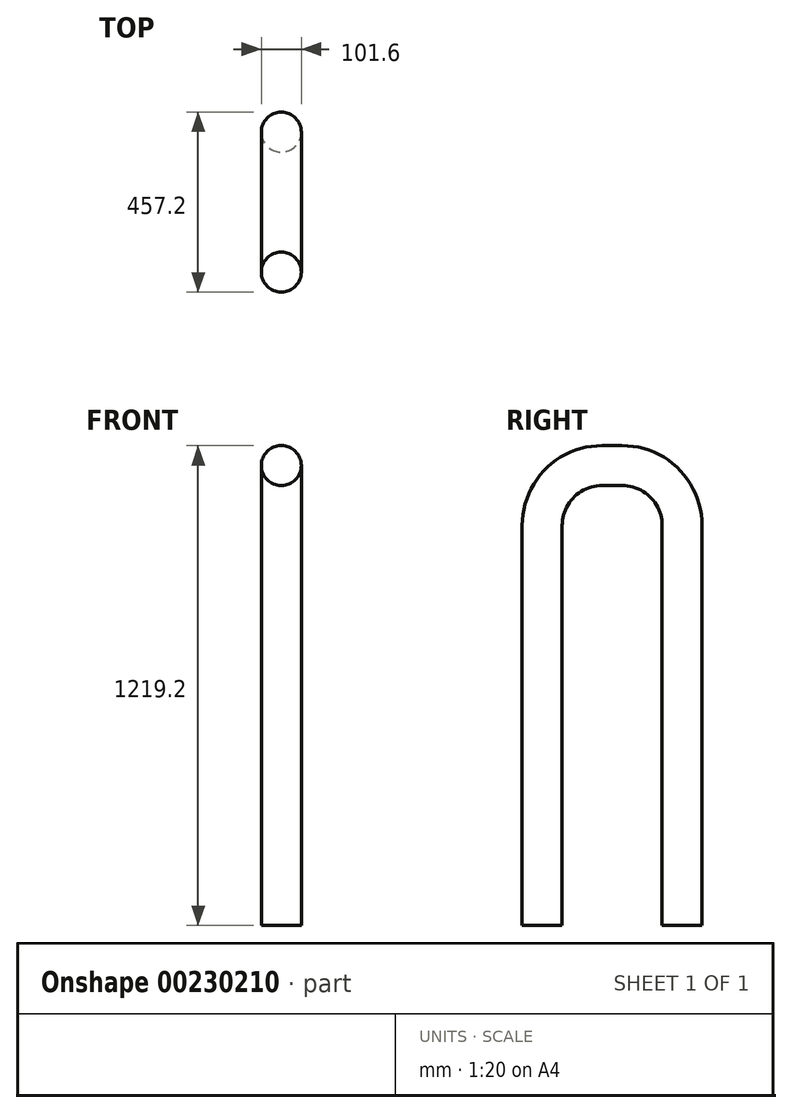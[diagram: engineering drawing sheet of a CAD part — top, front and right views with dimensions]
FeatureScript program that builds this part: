
annotation { "Feature Type Name" : "Feature", "Feature Type Description" : "" }
export const myFeature = defineFeature(function(context is Context, id is Id, definition is map)
    precondition{}
    {
        {
            var Q0;
            Q0=qCreatedBy(makeId("Right.planeOp"),FACE);
            var sketch = newSketch(context, id + "F0", { "sketchPlane" : qUnion([Q0])});
            skLineSegment(sketch, "E0", {"start": v(-207.98, 0) * mm, "end": v(-207.98, 1111.25) * mm});
            skLineSegment(sketch, "E1", {"start": v(-201.63, 1117.6) * mm, "end": v(46.02, 1117.6) * mm});
            skLineSegment(sketch, "E2", {"start": v(46.02, 1117.6) * mm, "end": v(46.02, 0) * mm});
            skLineSegment(sketch, "E3", {"start": v(46.02, 0) * mm, "end": v(147.62, 0) * mm});
            skLineSegment(sketch, "E4", {"start": v(147.62, 0) * mm, "end": v(147.62, 1219.2) * mm});
            skLineSegment(sketch, "E5", {"start": v(147.62, 1219.2) * mm, "end": v(-309.58, 1219.2) * mm});
            skLineSegment(sketch, "E6", {"start": v(-309.58, 1219.2) * mm, "end": v(-309.58, 0) * mm});
            skLineSegment(sketch, "E7", {"start": v(-309.58, 0) * mm, "end": v(-207.98, 0) * mm});
            skPoint(sketch, "E8.visualSharp", {"position": v(-207.98, 1117.6) * mm});
            skLineSegment(sketch, "E9", {"start": v(-207.98, 1111.25) * mm, "end": v(-207.98, 1117.6) * mm});
            skLineSegment(sketch, "E10", {"start": v(-201.63, 1117.6) * mm, "end": v(-207.98, 1117.6) * mm});
            skSolve(sketch);
        }
        {
            var Q0;
            Q0=qSketchRegion(id+"F0",true);
            extrude(context, id + "F1", {"entities" : qUnion([Q0]), "depth" : 101.6 * mm});
        }
        {
            var Q0;
            Q0=makeQuery(id+"F1.opExtrude","SWEPT_EDGE",EDGE,{"disambiguationData":[OSD([sQuery(id+"F0.wireOp",EDGE,"E9"),sQuery(id+"F0.wireOp",EDGE,"E10")])]});
            var Q1;
            Q1=makeQuery(id+"F1.opExtrude","SWEPT_EDGE",EDGE,{"disambiguationData":[OSD([sQuery(id+"F0.wireOp",EDGE,"E1"),sQuery(id+"F0.wireOp",EDGE,"E2")])]});
            fillet(context, id + "F2", {"entities" : qUnion([Q0, Q1]), "radius" : 101.6 * mm, "tangentPropagation" : true, "allowEdgeOverflow" : false});
        }
        {
            var Q0;
            Q0=makeQuery(id+"F1.opExtrude","SWEPT_EDGE",EDGE,{"disambiguationData":[OSD([sQuery(id+"F0.wireOp",EDGE,"E5"),sQuery(id+"F0.wireOp",EDGE,"E6")])]});
            var Q1;
            Q1=makeQuery(id+"F1.opExtrude","SWEPT_EDGE",EDGE,{"disambiguationData":[OSD([sQuery(id+"F0.wireOp",EDGE,"E4"),sQuery(id+"F0.wireOp",EDGE,"E5")])]});
            fillet(context, id + "F3", {"entities" : qUnion([Q0, Q1]), "radius" : 203.2 * mm, "tangentPropagation" : true, "allowEdgeOverflow" : false});
        }
        {
            var Q0;
            Q0=makeQuery(id+"F1.opExtrude","CAP_EDGE",EDGE,{"disambiguationData":[OSD([sQuery(id+"F0.wireOp",EDGE,"E0"),sQuery(id+"F0.wireOp",EDGE,"E9")])],"isStart":false});
            var Q1;
            Q1=makeQuery(id+"F1.opExtrude","CAP_EDGE",EDGE,{"disambiguationData":[OSD([sQuery(id+"F0.wireOp",EDGE,"E6")])],"isStart":false});
            var Q2;
            Q2=makeQuery(id+"F1.opExtrude","CAP_EDGE",EDGE,{"disambiguationData":[OSD([sQuery(id+"F0.wireOp",EDGE,"E6")])],"isStart":true});
            var Q3;
            Q3=makeQuery(id+"F1.opExtrude","CAP_EDGE",EDGE,{"disambiguationData":[OSD([sQuery(id+"F0.wireOp",EDGE,"E0"),sQuery(id+"F0.wireOp",EDGE,"E9")])],"isStart":true});
            fillet(context, id + "F4", {"entities" : qUnion([Q0, Q1, Q2, Q3]), "radius" : 50.8 * mm, "tangentPropagation" : true, "allowEdgeOverflow" : false});
        }
    });
